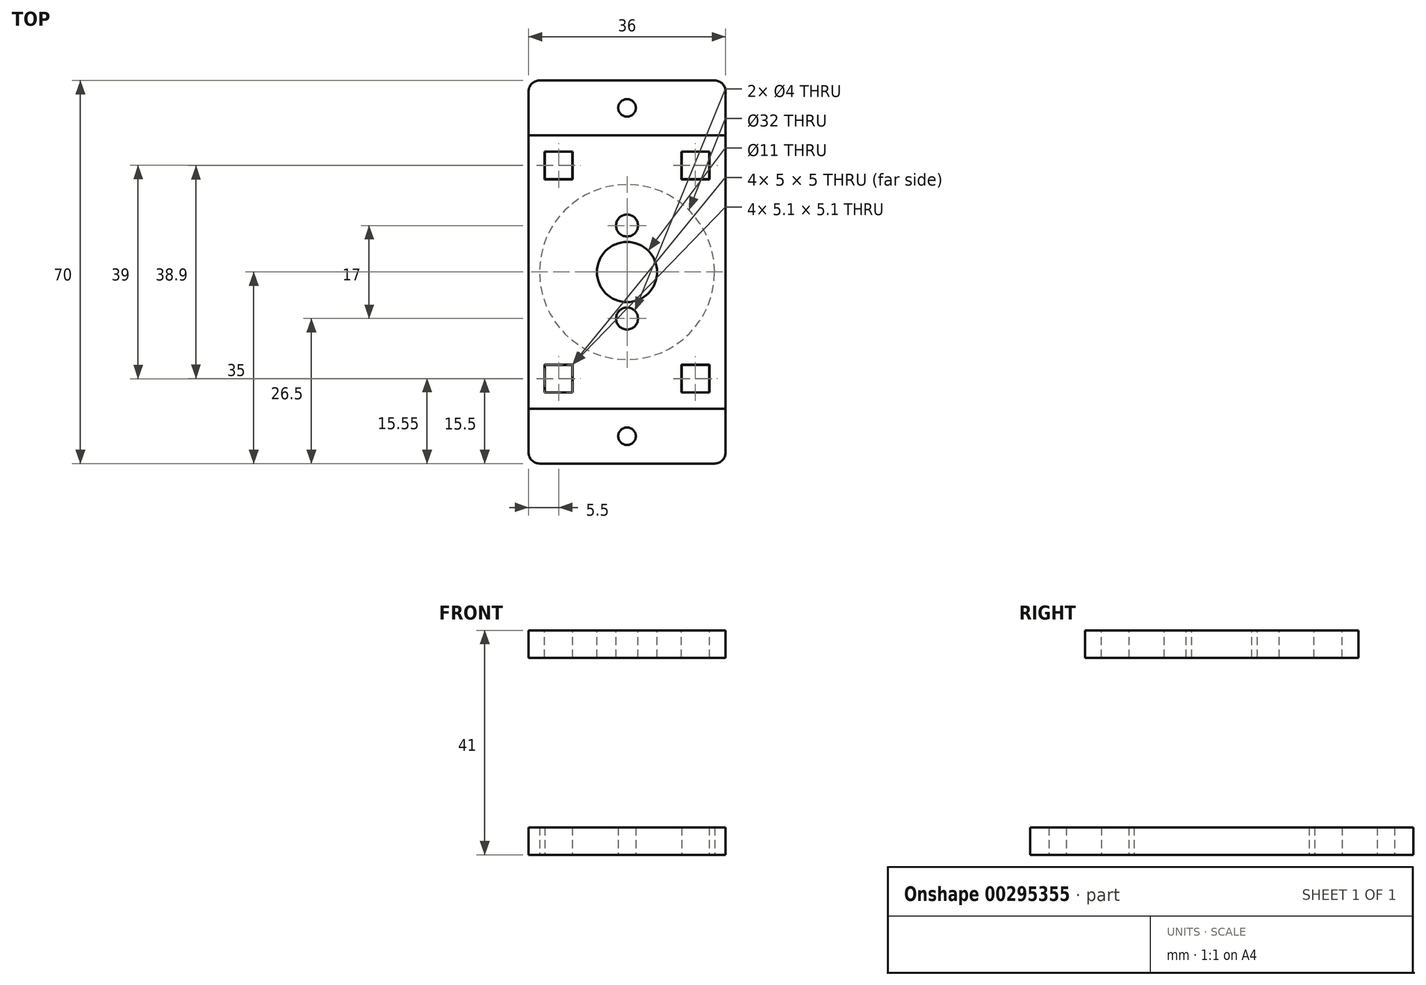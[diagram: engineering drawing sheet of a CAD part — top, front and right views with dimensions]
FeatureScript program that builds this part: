
annotation { "Feature Type Name" : "Feature", "Feature Type Description" : "" }
export const myFeature = defineFeature(function(context is Context, id is Id, definition is map)
    precondition{}
    {
        {
            var Q0;
            Q0=qCreatedBy(makeId("Top.planeOp"),FACE);
            var sketch = newSketch(context, id + "F0", { "sketchPlane" : qUnion([Q0])});
            skLineSegment(sketch, "E0.bottom", {"start": v(16, 35) * mm, "end": v(-16, 35) * mm});
            skLineSegment(sketch, "E0.top", {"start": v(16, -35) * mm, "end": v(-16, -35) * mm});
            skLineSegment(sketch, "E0.left", {"start": v(18, 33) * mm, "end": v(18, -33) * mm});
            skLineSegment(sketch, "E0.right", {"start": v(-18, 33) * mm, "end": v(-18, -33) * mm});
            skCircle(sketch, "E1", {"center": v(0, -30) * mm, "radius": 1.6 * mm});
            skCircle(sketch, "E2.MirrorC", {"center": v(0, 30) * mm, "radius": 1.6 * mm});
            skPoint(sketch, "E3.visualSharp", {"position": v(-18, 35) * mm});
            skArc(sketch, "E3.filletArc", {"start": v(-16, 35) * mm, "mid": v(-17.41, 34.41) * mm, "end": v(-18, 33) * mm});
            skPoint(sketch, "E4.visualSharp", {"position": v(18, 35) * mm});
            skArc(sketch, "E4.filletArc", {"start": v(18, 33) * mm, "mid": v(17.41, 34.41) * mm, "end": v(16, 35) * mm});
            skPoint(sketch, "E5.visualSharp", {"position": v(18, -35) * mm});
            skArc(sketch, "E5.filletArc", {"start": v(16, -35) * mm, "mid": v(17.41, -34.41) * mm, "end": v(18, -33) * mm});
            skPoint(sketch, "E6.visualSharp", {"position": v(-18, -35) * mm});
            skArc(sketch, "E6.filletArc", {"start": v(-18, -33) * mm, "mid": v(-17.41, -34.41) * mm, "end": v(-16, -35) * mm});
            skLineSegment(sketch, "E7.bottom", {"start": v(-15, 22) * mm, "end": v(-10, 22) * mm});
            skLineSegment(sketch, "E7.top", {"start": v(-15, 17) * mm, "end": v(-10, 17) * mm});
            skLineSegment(sketch, "E7.left", {"start": v(-15, 22) * mm, "end": v(-15, 17) * mm});
            skLineSegment(sketch, "E7.right", {"start": v(-10, 22) * mm, "end": v(-10, 17) * mm});
            skLineSegment(sketch, "E8.bottom", {"start": v(10, 22) * mm, "end": v(15, 22) * mm});
            skLineSegment(sketch, "E8.top", {"start": v(10, 17) * mm, "end": v(15, 17) * mm});
            skLineSegment(sketch, "E8.left", {"start": v(10, 22) * mm, "end": v(10, 17) * mm});
            skLineSegment(sketch, "E8.right", {"start": v(15, 22) * mm, "end": v(15, 17) * mm});
            skLineSegment(sketch, "E9.bottom", {"start": v(-15, -17) * mm, "end": v(-10, -17) * mm});
            skLineSegment(sketch, "E9.top", {"start": v(-15, -22) * mm, "end": v(-10, -22) * mm});
            skLineSegment(sketch, "E9.left", {"start": v(-15, -17) * mm, "end": v(-15, -22) * mm});
            skLineSegment(sketch, "E9.right", {"start": v(-10, -17) * mm, "end": v(-10, -22) * mm});
            skLineSegment(sketch, "E10.bottom", {"start": v(10, -17) * mm, "end": v(15, -17) * mm});
            skLineSegment(sketch, "E10.top", {"start": v(10, -22) * mm, "end": v(15, -22) * mm});
            skLineSegment(sketch, "E10.left", {"start": v(10, -17) * mm, "end": v(10, -22) * mm});
            skLineSegment(sketch, "E10.right", {"start": v(15, -17) * mm, "end": v(15, -22) * mm});
            skCircle(sketch, "E11", {"center": v(0, 0) * mm, "radius": 16 * mm});
            skSolve(sketch);
        }
        {
            var Q0;
            Q0=qCreatedBy(makeId("Top.planeOp"),FACE);
            cPlane(context, id + "F1", {"entities" : qUnion([Q0]), "cplaneType" : CPlaneType.OFFSET, "offset" : 41 * mm, "width" : 150 * mm, "height" : 150 * mm});
        }
        {
            var Q0;
            Q0=qCreatedBy(id+"F1.planeOp",FACE);
            var sketch = newSketch(context, id + "F2", { "sketchPlane" : qUnion([Q0])});
            skPoint(sketch, "E12.middle", {"position": v(0, 0) * mm});
            skPoint(sketch, "E13", {"position": v(0, -8.5) * mm});
            skPoint(sketch, "E14", {"position": v(0, 8.5) * mm});
            skCircle(sketch, "E15", {"center": v(0, 8.5) * mm, "radius": 2 * mm});
            skCircle(sketch, "E16", {"center": v(0, -8.5) * mm, "radius": 2 * mm});
            skCircle(sketch, "E17", {"center": v(0, 0) * mm, "radius": 5.5 * mm});
            skLineSegment(sketch, "E18.bottom", {"start": v(18, -25) * mm, "end": v(-18, -25) * mm});
            skLineSegment(sketch, "E18.top", {"start": v(18, 25) * mm, "end": v(-18, 25) * mm});
            skLineSegment(sketch, "E18.left", {"start": v(18, -25) * mm, "end": v(18, 25) * mm});
            skLineSegment(sketch, "E18.right", {"start": v(-18, -25) * mm, "end": v(-18, 25) * mm});
            skLineSegment(sketch, "E19.bottom", {"start": v(-15.05, 22) * mm, "end": v(-9.95, 22) * mm});
            skLineSegment(sketch, "E19.top", {"start": v(-15.05, 16.9) * mm, "end": v(-9.95, 16.9) * mm});
            skLineSegment(sketch, "E19.left", {"start": v(-15.05, 22) * mm, "end": v(-15.05, 16.9) * mm});
            skLineSegment(sketch, "E19.right", {"start": v(-9.95, 22) * mm, "end": v(-9.95, 16.9) * mm});
            skLineSegment(sketch, "E20.bottom", {"start": v(9.95, 22) * mm, "end": v(15.05, 22) * mm});
            skLineSegment(sketch, "E20.top", {"start": v(9.95, 16.9) * mm, "end": v(15.05, 16.9) * mm});
            skLineSegment(sketch, "E20.left", {"start": v(9.95, 22) * mm, "end": v(9.95, 16.9) * mm});
            skLineSegment(sketch, "E20.right", {"start": v(15.05, 22) * mm, "end": v(15.05, 16.9) * mm});
            skLineSegment(sketch, "E21.bottom", {"start": v(-15.05, -16.9) * mm, "end": v(-9.95, -16.9) * mm});
            skLineSegment(sketch, "E21.top", {"start": v(-15.05, -22) * mm, "end": v(-9.95, -22) * mm});
            skLineSegment(sketch, "E21.left", {"start": v(-15.05, -16.9) * mm, "end": v(-15.05, -22) * mm});
            skLineSegment(sketch, "E21.right", {"start": v(-9.95, -16.9) * mm, "end": v(-9.95, -22) * mm});
            skLineSegment(sketch, "E22.bottom", {"start": v(9.95, -16.9) * mm, "end": v(15.05, -16.9) * mm});
            skLineSegment(sketch, "E22.top", {"start": v(9.95, -22) * mm, "end": v(15.05, -22) * mm});
            skLineSegment(sketch, "E22.left", {"start": v(9.95, -16.9) * mm, "end": v(9.95, -22) * mm});
            skLineSegment(sketch, "E22.right", {"start": v(15.05, -16.9) * mm, "end": v(15.05, -22) * mm});
            skLineSegment(sketch, "E23", {"start": v(-15, -38.58) * mm, "end": v(-10, -38.58) * mm});
            skLineSegment(sketch, "E24", {"start": v(-10, -38.58) * mm, "end": v(-10, -43.58) * mm});
            skLineSegment(sketch, "E25", {"start": v(-10, -43.58) * mm, "end": v(10, -43.58) * mm});
            skLineSegment(sketch, "E26", {"start": v(10, -43.58) * mm, "end": v(10, -38.58) * mm});
            skLineSegment(sketch, "E27", {"start": v(10, -38.58) * mm, "end": v(15, -38.58) * mm});
            skLineSegment(sketch, "E28", {"start": v(15, -38.58) * mm, "end": v(15, -43.58) * mm});
            skLineSegment(sketch, "E29", {"start": v(15, -43.58) * mm, "end": v(18, -43.58) * mm});
            skLineSegment(sketch, "E30", {"start": v(18, -43.58) * mm, "end": v(18, -84.58) * mm});
            skLineSegment(sketch, "E31", {"start": v(-18, -84.58) * mm, "end": v(-18, -43.58) * mm});
            skLineSegment(sketch, "E32", {"start": v(-18, -43.58) * mm, "end": v(-15, -43.58) * mm});
            skLineSegment(sketch, "E33", {"start": v(-15, -43.58) * mm, "end": v(-15, -38.58) * mm});
            skLineSegment(sketch, "E34", {"start": v(18, -84.58) * mm, "end": v(15, -84.58) * mm});
            skLineSegment(sketch, "E35", {"start": v(15, -84.58) * mm, "end": v(15, -89.58) * mm});
            skLineSegment(sketch, "E36", {"start": v(15, -89.58) * mm, "end": v(10, -89.58) * mm});
            skLineSegment(sketch, "E37", {"start": v(10, -89.58) * mm, "end": v(10, -84.58) * mm});
            skLineSegment(sketch, "E38", {"start": v(10, -84.58) * mm, "end": v(-10, -84.58) * mm});
            skLineSegment(sketch, "E39", {"start": v(-10, -84.58) * mm, "end": v(-10, -89.58) * mm});
            skLineSegment(sketch, "E40", {"start": v(-10, -89.58) * mm, "end": v(-15, -89.58) * mm});
            skLineSegment(sketch, "E41", {"start": v(-15, -89.58) * mm, "end": v(-15, -84.58) * mm});
            skLineSegment(sketch, "E42", {"start": v(-15, -84.58) * mm, "end": v(-18, -84.58) * mm});
            skPoint(sketch, "E43", {"position": v(0, -43.58) * mm});
            skLineSegment(sketch, "E44", {"start": v(-15, -92.24) * mm, "end": v(-10, -92.24) * mm});
            skLineSegment(sketch, "E45", {"start": v(-10, -92.24) * mm, "end": v(-10, -97.24) * mm});
            skLineSegment(sketch, "E46", {"start": v(-10, -97.24) * mm, "end": v(10, -97.24) * mm});
            skLineSegment(sketch, "E47", {"start": v(10, -97.24) * mm, "end": v(10, -92.24) * mm});
            skLineSegment(sketch, "E48", {"start": v(10, -92.24) * mm, "end": v(15, -92.24) * mm});
            skLineSegment(sketch, "E49", {"start": v(15, -92.24) * mm, "end": v(15, -97.24) * mm});
            skLineSegment(sketch, "E50", {"start": v(15, -97.24) * mm, "end": v(18, -97.24) * mm});
            skLineSegment(sketch, "E51", {"start": v(18, -97.24) * mm, "end": v(18, -138.24) * mm});
            skLineSegment(sketch, "E52", {"start": v(-18, -138.24) * mm, "end": v(-18, -97.24) * mm});
            skLineSegment(sketch, "E53", {"start": v(-18, -97.24) * mm, "end": v(-15, -97.24) * mm});
            skLineSegment(sketch, "E54", {"start": v(-15, -97.24) * mm, "end": v(-15, -92.24) * mm});
            skLineSegment(sketch, "E55", {"start": v(18, -138.24) * mm, "end": v(15, -138.24) * mm});
            skLineSegment(sketch, "E56", {"start": v(15, -138.24) * mm, "end": v(15, -143.24) * mm});
            skLineSegment(sketch, "E57", {"start": v(15, -143.24) * mm, "end": v(10, -143.24) * mm});
            skLineSegment(sketch, "E58", {"start": v(10, -143.24) * mm, "end": v(10, -138.24) * mm});
            skLineSegment(sketch, "E59", {"start": v(10, -138.24) * mm, "end": v(-10, -138.24) * mm});
            skLineSegment(sketch, "E60", {"start": v(-10, -138.24) * mm, "end": v(-10, -143.24) * mm});
            skLineSegment(sketch, "E61", {"start": v(-10, -143.24) * mm, "end": v(-15, -143.24) * mm});
            skLineSegment(sketch, "E62", {"start": v(-15, -143.24) * mm, "end": v(-15, -138.24) * mm});
            skLineSegment(sketch, "E63", {"start": v(-15, -138.24) * mm, "end": v(-18, -138.24) * mm});
            skPoint(sketch, "E64", {"position": v(0, -97.24) * mm});
            skSolve(sketch);
        }
        {
            var Q0;
            Q0=makeQuery(id+"F0.imprint","IMPRINT",FACE,{"disambiguationData":[TD([[makeQuery(id+"F0.imprint","IMPRINT",EDGE,{"derivedFrom":sQuery(id+"F0.wireOp",EDGE,"E0.bottom")}),1.0]])]});
            extrude(context, id + "F3", {"entities" : qUnion([Q0]), "depth" : 5 * mm});
        }
        {
            var Q0;
            Q0=makeQuery(id+"F2.imprint","IMPRINT",FACE,{"disambiguationData":[TD([[makeQuery(id+"F2.imprint","IMPRINT",EDGE,{"derivedFrom":sQuery(id+"F2.wireOp",EDGE,"E15")}),-1.0]])]});
            extrude(context, id + "F4", {"entities" : qUnion([Q0]), "oppositeDirection" : true, "depth" : 5 * mm});
        }
    });
